# Revit family: FONESTAR_Proyector_Sonido_EN-54
name_source: partatom
category: Communication Devices
units: mm (PartAtom-declared; Revit-internal decimal feet)

## family parameters
Always vertical = No
Cut with Voids When Loaded = No
Maintain Annotation Orientation = No
Part Type = Normal
Room Calculation Point = No
Round Connector Dimension = Use Diameter
Shared = No
Work Plane-Based = Yes

## types (2) — shared parameters
Cuerpo.Diámetro.Interior = 140 mm  [stored 0.459318 ft]
Cuerpo.Material = Acero - Blanco RAL(9010)
Default Elevation = 1000 mm  [stored 3.28084 ft]
Diámetro = 146 mm  [stored 0.479003 ft]
Lente.Espesor = 5 mm  [stored 0.0164042 ft]
Manufacturer = FONESTAR
Model = PF-53T-EN
Modified by = XPV
Potencia Acústica = 20 W RMS
Protección IP = IP-66
Rejilla.Espesor = 2 mm  [stored 0.00656168 ft]
Rejilla.Material = Acero_Rejilla - Blanco RAL(9010)
Respuesta Acústica = 130-20.000 Hz
Reviewed by = TAG
Soporte.Espesor = 3 mm  [stored 0.00984252 ft]
Soporte.Material = Acero - Blanco RAL(9010)
URL = https://fonestar.com
URL.Product = https://fonestar.com
Version = R1

## per-type parameters (varying)
| type | Altura | Description | Longitud | Peso | Soporte.Altura | Soporte.Especial | Soporte.Longitud | Soporte.U |
| PF-53T-EN | 141 mm | Proyector de sonido EN 54 con transformador de línea 100 V. | 207 mm  [stored 0.679134 ft] | 2,5 Kg | 156 mm | No | 30 mm  [stored 0.0984252 ft] | Yes |
| PF-54TD-EN | 93 mm  [stored 0.305118 ft] | Proyector de sonido bidireccional EN 54 con transformador de línea 100 V. | 186 mm | 3,3 Kg | 143 mm | Yes | 100 mm  [stored 0.328084 ft] | No |

note: [stored X ft] marks values corroborated as IEEE doubles in the binary element streams (Revit-internal decimal feet)
